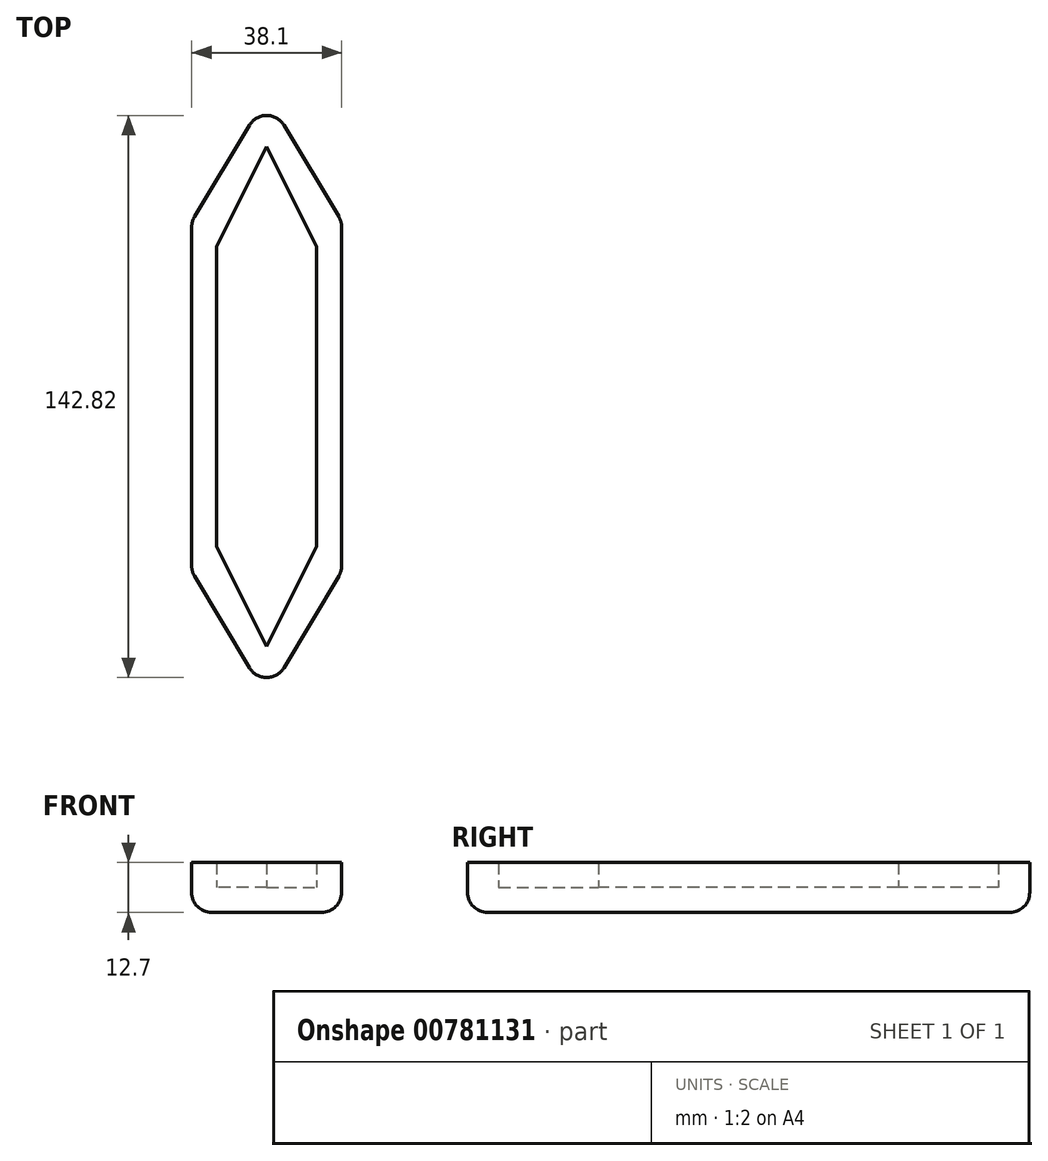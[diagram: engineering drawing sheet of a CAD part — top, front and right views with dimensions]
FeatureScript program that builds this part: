
annotation { "Feature Type Name" : "Feature", "Feature Type Description" : "" }
export const myFeature = defineFeature(function(context is Context, id is Id, definition is map)
    precondition{}
    {
        {
            var Q0;
            Q0=qCreatedBy(makeId("Top.planeOp"),FACE);
            var sketch = newSketch(context, id + "F0", { "sketchPlane" : qUnion([Q0])});
            skLineSegment(sketch, "E0.left", {"start": v(12.7, 38.1) * mm, "end": v(12.7, -38.1) * mm});
            skLineSegment(sketch, "E0.right", {"start": v(-12.7, 38.1) * mm, "end": v(-12.7, -38.1) * mm});
            skPoint(sketch, "E0.middle", {"position": v(0, 0) * mm});
            skLineSegment(sketch, "E1", {"start": v(0, -63.5) * mm, "end": v(-12.7, -38.1) * mm});
            skLineSegment(sketch, "E2", {"start": v(0, -63.5) * mm, "end": v(12.7, -38.1) * mm});
            skLineSegment(sketch, "E3", {"start": v(0, 63.5) * mm, "end": v(-12.7, 38.1) * mm});
            skLineSegment(sketch, "E4", {"start": v(0, 63.5) * mm, "end": v(12.7, 38.1) * mm});
            skLineSegment(sketch, "E5.bottom", {"start": v(19.05, 44.45) * mm, "end": v(-19.05, 44.45) * mm});
            skLineSegment(sketch, "E5.top", {"start": v(19.05, -44.45) * mm, "end": v(-19.05, -44.45) * mm});
            skLineSegment(sketch, "E5.left", {"start": v(19.05, 44.45) * mm, "end": v(19.05, -44.45) * mm});
            skLineSegment(sketch, "E5.right", {"start": v(-19.05, 44.45) * mm, "end": v(-19.05, -44.45) * mm});
            skLineSegment(sketch, "E6", {"start": v(0, 44.45) * mm, "end": v(0, 76.2) * mm});
            skLineSegment(sketch, "E7", {"start": v(0, 76.2) * mm, "end": v(-19.05, 44.45) * mm});
            skLineSegment(sketch, "E8", {"start": v(0, 76.2) * mm, "end": v(19.05, 44.45) * mm});
            skLineSegment(sketch, "E9", {"start": v(0, -44.45) * mm, "end": v(0, -76.2) * mm});
            skLineSegment(sketch, "E10", {"start": v(0, -76.2) * mm, "end": v(-19.05, -44.45) * mm});
            skLineSegment(sketch, "E11", {"start": v(0, -76.2) * mm, "end": v(19.05, -44.45) * mm});
            skLineSegment(sketch, "E12", {"start": v(-12.7, -38.1) * mm, "end": v(12.7, -38.1) * mm});
            skLineSegment(sketch, "E13", {"start": v(0, -63.5) * mm, "end": v(0, -38.1) * mm});
            skLineSegment(sketch, "E14", {"start": v(-12.7, 38.1) * mm, "end": v(12.7, 38.1) * mm});
            skLineSegment(sketch, "E15", {"start": v(0, 38.1) * mm, "end": v(0, 63.5) * mm});
            skSolve(sketch);
        }
        {
            var Q0;
            {var subQ5=sQuery(id+"F0.wireOp",EDGE,"E7");Q0=makeQuery(id+"F0.imprint","IMPRINT",FACE,{"disambiguationData":[TD([[makeQuery(id+"F0.imprint","IMPRINT",EDGE,{"derivedFrom":subQ5}),1.0]])]});}
            var Q1;
            {var subQ5=sQuery(id+"F0.wireOp",EDGE,"E8");Q1=makeQuery(id+"F0.imprint","IMPRINT",FACE,{"disambiguationData":[TD([[makeQuery(id+"F0.imprint","IMPRINT",EDGE,{"derivedFrom":subQ5}),-1.0]])]});}
            var Q2;
            {var subQ1=sQuery(id+"F0.wireOp",EDGE,"E0.left");Q2=makeQuery(id+"F0.imprint","IMPRINT",FACE,{"disambiguationData":[TD([[makeQuery(id+"F0.imprint","IMPRINT",EDGE,{"derivedFrom":subQ1}),1.0]])]});}
            var Q3;
            {var subQ1=sQuery(id+"F0.wireOp",EDGE,"E0.right");Q3=makeQuery(id+"F0.imprint","IMPRINT",FACE,{"disambiguationData":[TD([[makeQuery(id+"F0.imprint","IMPRINT",EDGE,{"derivedFrom":subQ1}),-1.0]])]});}
            var Q4;
            {var subQ5=sQuery(id+"F0.wireOp",EDGE,"E10");Q4=makeQuery(id+"F0.imprint","IMPRINT",FACE,{"disambiguationData":[TD([[makeQuery(id+"F0.imprint","IMPRINT",EDGE,{"derivedFrom":subQ5}),-1.0]])]});}
            var Q5;
            {var subQ5=sQuery(id+"F0.wireOp",EDGE,"E11");Q5=makeQuery(id+"F0.imprint","IMPRINT",FACE,{"disambiguationData":[TD([[makeQuery(id+"F0.imprint","IMPRINT",EDGE,{"derivedFrom":subQ5}),1.0]])]});}
            extrude(context, id + "F1", {"entities" : qUnion([Q0, Q1, Q2, Q3, Q4, Q5]), "depth" : 12.7 * mm, "offsetDistance" : 25.4 * mm});
        }
        {
            var Q0;
            {var subQ1=sQuery(id+"F0.wireOp",EDGE,"E4");var subQ3=sQuery(id+"F0.wireOp",EDGE,"E5.bottom");var subQ4=makeQuery(id+"F0.imprint","INTERSECT",VERTEX,{"derivedFrom":[subQ1,subQ3]});Q0=makeQuery(id+"F0.imprint","IMPRINT",FACE,{"disambiguationData":[TD([[makeQuery(id+"F0.imprint","IMPRINT",EDGE,{"disambiguationData":[TD([[subQ4,1.0]])],"derivedFrom":subQ1}),-1.0]])]});}
            var Q1;
            {var subQ1=sQuery(id+"F0.wireOp",EDGE,"E3");var subQ3=sQuery(id+"F0.wireOp",EDGE,"E5.bottom");var subQ4=makeQuery(id+"F0.imprint","INTERSECT",VERTEX,{"derivedFrom":[subQ1,subQ3]});Q1=makeQuery(id+"F0.imprint","IMPRINT",FACE,{"disambiguationData":[TD([[makeQuery(id+"F0.imprint","IMPRINT",EDGE,{"disambiguationData":[TD([[subQ4,1.0]])],"derivedFrom":subQ1}),1.0]])]});}
            var Q2;
            {var subQ5=sQuery(id+"F0.wireOp",EDGE,"E15");Q2=makeQuery(id+"F0.imprint","IMPRINT",FACE,{"disambiguationData":[TD([[makeQuery(id+"F0.imprint","IMPRINT",EDGE,{"derivedFrom":subQ5}),1.0]])]});}
            var Q3;
            {var subQ5=sQuery(id+"F0.wireOp",EDGE,"E15");Q3=makeQuery(id+"F0.imprint","IMPRINT",FACE,{"disambiguationData":[TD([[makeQuery(id+"F0.imprint","IMPRINT",EDGE,{"derivedFrom":subQ5}),-1.0]])]});}
            var Q4;
            {var subQ1=sQuery(id+"F0.wireOp",EDGE,"E0.left");Q4=makeQuery(id+"F0.imprint","IMPRINT",FACE,{"disambiguationData":[TD([[makeQuery(id+"F0.imprint","IMPRINT",EDGE,{"derivedFrom":subQ1}),-1.0]])]});}
            var Q5;
            {var subQ5=sQuery(id+"F0.wireOp",EDGE,"E13");Q5=makeQuery(id+"F0.imprint","IMPRINT",FACE,{"disambiguationData":[TD([[makeQuery(id+"F0.imprint","IMPRINT",EDGE,{"derivedFrom":subQ5}),-1.0]])]});}
            var Q6;
            {var subQ5=sQuery(id+"F0.wireOp",EDGE,"E13");Q6=makeQuery(id+"F0.imprint","IMPRINT",FACE,{"disambiguationData":[TD([[makeQuery(id+"F0.imprint","IMPRINT",EDGE,{"derivedFrom":subQ5}),1.0]])]});}
            var Q7;
            {var subQ1=sQuery(id+"F0.wireOp",EDGE,"E1");var subQ3=sQuery(id+"F0.wireOp",EDGE,"E5.top");var subQ4=makeQuery(id+"F0.imprint","INTERSECT",VERTEX,{"derivedFrom":[subQ1,subQ3]});Q7=makeQuery(id+"F0.imprint","IMPRINT",FACE,{"disambiguationData":[TD([[makeQuery(id+"F0.imprint","IMPRINT",EDGE,{"disambiguationData":[TD([[subQ4,1.0]])],"derivedFrom":subQ1}),-1.0]])]});}
            var Q8;
            {var subQ1=sQuery(id+"F0.wireOp",EDGE,"E2");var subQ3=sQuery(id+"F0.wireOp",EDGE,"E5.top");var subQ4=makeQuery(id+"F0.imprint","INTERSECT",VERTEX,{"derivedFrom":[subQ1,subQ3]});Q8=makeQuery(id+"F0.imprint","IMPRINT",FACE,{"disambiguationData":[TD([[makeQuery(id+"F0.imprint","IMPRINT",EDGE,{"disambiguationData":[TD([[subQ4,1.0]])],"derivedFrom":subQ1}),1.0]])]});}
            extrude(context, id + "F2", {"entities" : qUnion([Q0, Q1, Q2, Q3, Q4, Q5, Q6, Q7, Q8]), "operationType" : NewBodyOperationType.ADD, "depth" : 6.35 * mm, "offsetDistance" : 25.4 * mm});
        }
        {
            var Q0;
            Q0=makeQuery(id+"F1.opExtrude","SWEPT_EDGE",EDGE,{"disambiguationData":[OSD([sQuery(id+"F0.wireOp",EDGE,"E5.top"),sQuery(id+"F0.wireOp",EDGE,"E5.left"),sQuery(id+"F0.wireOp",EDGE,"E11")])]});
            var Q1;
            Q1=makeQuery(id+"F1.opExtrude","SWEPT_EDGE",EDGE,{"disambiguationData":[OSD([sQuery(id+"F0.wireOp",EDGE,"E9"),sQuery(id+"F0.wireOp",EDGE,"E10"),sQuery(id+"F0.wireOp",EDGE,"E11")])]});
            var Q2;
            Q2=makeQuery(id+"F1.opExtrude","SWEPT_EDGE",EDGE,{"disambiguationData":[OSD([sQuery(id+"F0.wireOp",EDGE,"E5.top"),sQuery(id+"F0.wireOp",EDGE,"E5.right"),sQuery(id+"F0.wireOp",EDGE,"E10")])]});
            var Q3;
            Q3=makeQuery(id+"F1.opExtrude","SWEPT_EDGE",EDGE,{"disambiguationData":[OSD([sQuery(id+"F0.wireOp",EDGE,"E5.bottom"),sQuery(id+"F0.wireOp",EDGE,"E5.right"),sQuery(id+"F0.wireOp",EDGE,"E7")])]});
            var Q4;
            Q4=makeQuery(id+"F1.opExtrude","SWEPT_EDGE",EDGE,{"disambiguationData":[OSD([sQuery(id+"F0.wireOp",EDGE,"E6"),sQuery(id+"F0.wireOp",EDGE,"E7"),sQuery(id+"F0.wireOp",EDGE,"E8")])]});
            var Q5;
            Q5=makeQuery(id+"F1.opExtrude","SWEPT_EDGE",EDGE,{"disambiguationData":[OSD([sQuery(id+"F0.wireOp",EDGE,"E5.bottom"),sQuery(id+"F0.wireOp",EDGE,"E5.left"),sQuery(id+"F0.wireOp",EDGE,"E8")])]});
            fillet(context, id + "F3", {"entities" : qUnion([Q0, Q1, Q2, Q3, Q4, Q5]), "radius" : 5.08 * mm, "tangentPropagation" : true, "allowEdgeOverflow" : false});
        }
        {
            var Q0;
            Q0=makeQuery(id+"F1.opExtrude","CAP_EDGE",EDGE,{"disambiguationData":[OSD([sQuery(id+"F0.wireOp",EDGE,"E5.right")])],"isStart":true});
            fillet(context, id + "F4", {"entities" : qUnion([Q0]), "radius" : 5.08 * mm, "tangentPropagation" : true, "allowEdgeOverflow" : false});
        }
    });
